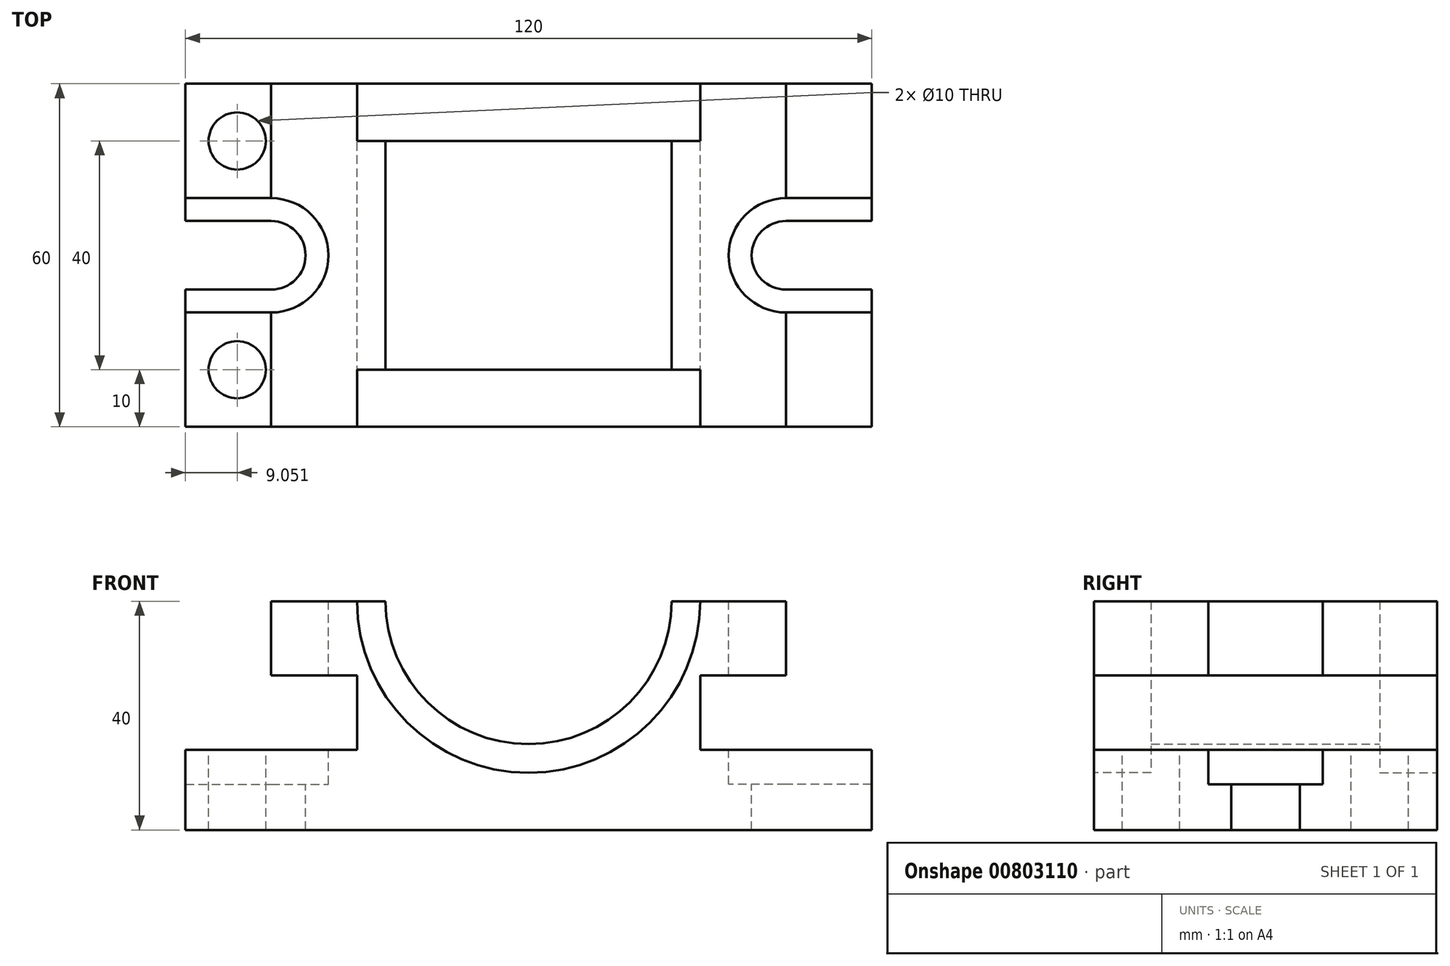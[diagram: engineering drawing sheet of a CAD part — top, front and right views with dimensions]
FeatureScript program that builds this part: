
annotation { "Feature Type Name" : "Feature", "Feature Type Description" : "" }
export const myFeature = defineFeature(function(context is Context, id is Id, definition is map)
    precondition{}
    {
        {
            var Q0;
            Q0=qCreatedBy(makeId("Front.planeOp"),FACE);
            var sketch = newSketch(context, id + "F0", { "sketchPlane" : qUnion([Q0])});
            skLineSegment(sketch, "E0.bottom", {"start": v(45, 20) * mm, "end": v(25, 20) * mm});
            skLineSegment(sketch, "E0.top", {"start": v(60, -20) * mm, "end": v(-60, -20) * mm});
            skLineSegment(sketch, "E0.left", {"start": v(60, -6) * mm, "end": v(60, -20) * mm});
            skPoint(sketch, "E0.middle", {"position": v(0, 0) * mm});
            skLineSegment(sketch, "E1.bottom", {"start": v(-45, 7) * mm, "end": v(-30, 7) * mm});
            skLineSegment(sketch, "E1.top", {"start": v(-60, -6) * mm, "end": v(-30, -6) * mm});
            skLineSegment(sketch, "E1.right", {"start": v(-30, 7) * mm, "end": v(-30, -6) * mm});
            skLineSegment(sketch, "E2.trimOffspring", {"start": v(-60, -6) * mm, "end": v(-60, -20) * mm});
            skLineSegment(sketch, "E3", {"start": v(-45, 20) * mm, "end": v(-45, 7) * mm});
            skPoint(sketch, "E0.right.start.orphan", {"position": v(-60, 20) * mm});
            skLineSegment(sketch, "E4.MirrorCS", {"start": v(30, 7) * mm, "end": v(30, -6) * mm});
            skLineSegment(sketch, "E5.MirrorCS", {"start": v(45, 7) * mm, "end": v(30, 7) * mm});
            skLineSegment(sketch, "E6.MirrorCS", {"start": v(45, 20) * mm, "end": v(45, 7) * mm});
            skLineSegment(sketch, "E7.MirrorCS", {"start": v(60, -6) * mm, "end": v(30, -6) * mm});
            skPoint(sketch, "E8.orphan", {"position": v(60, 20) * mm});
            skArc(sketch, "E9", {"start": v(-25, 20) * mm, "mid": v(0, -5) * mm, "end": v(25, 20) * mm});
            skLineSegment(sketch, "E10.trimOffspring", {"start": v(-25, 20) * mm, "end": v(-45, 20) * mm});
            skSolve(sketch);
        }
        {
            var Q0;
            Q0 = qSketchRegion(id + "F0", true);
            extrude(context, id + "F1", {"entities" : qUnion([Q0]), "depth" : 30 * mm, "offsetDistance" : 25 * mm, "hasSecondDirection" : true, "secondDirectionOppositeDirection" : true, "secondDirectionDepth" : 30 * mm});
        }
        {
            var Q0;
            Q0=makeQuery(id+"F1.opExtrude","CAP_FACE",FACE,{"disambiguationData":[OSD([sQuery(id+"F0.wireOp",EDGE,"E0.bottom"),sQuery(id+"F0.wireOp",EDGE,"E0.top"),sQuery(id+"F0.wireOp",EDGE,"E1.bottom"),sQuery(id+"F0.wireOp",EDGE,"E1.top"),sQuery(id+"F0.wireOp",EDGE,"E1.right"),sQuery(id+"F0.wireOp",EDGE,"E2.trimOffspring"),sQuery(id+"F0.wireOp",EDGE,"E3"),sQuery(id+"F0.wireOp",EDGE,"E4.MirrorCS"),sQuery(id+"F0.wireOp",EDGE,"E5.MirrorCS"),sQuery(id+"F0.wireOp",EDGE,"E6.MirrorCS"),sQuery(id+"F0.wireOp",EDGE,"E7.MirrorCS"),sQuery(id+"F0.wireOp",EDGE,"E0.left"),sQuery(id+"F0.wireOp",EDGE,"E9"),sQuery(id+"F0.wireOp",EDGE,"E10.trimOffspring")])],"isStart":false});
            var sketch = newSketch(context, id + "F2", { "sketchPlane" : qUnion([Q0])});
            skArc(sketch, "E11", {"start": v(-30, 20) * mm, "mid": v(0, -10) * mm, "end": v(30, 20) * mm});
            skLineSegment(sketch, "E12", {"start": v(-30, 20) * mm, "end": v(30, 20) * mm});
            skSolve(sketch);
        }
        {
            var Q0;
            {var subQ0=sQuery(id+"F2.wireOp",EDGE,"E11");Q0=makeQuery(id+"F2.imprint","IMPRINT",FACE,{"disambiguationData":[TD([[makeQuery(id+"F2.imprint","IMPRINT",EDGE,{"derivedFrom":subQ0}),1.0]])]});}
            extrude(context, id + "F3", {"entities" : qUnion([Q0]), "operationType" : NewBodyOperationType.REMOVE, "oppositeDirection" : true, "depth" : 10 * mm, "offsetDistance" : 25 * mm});
        }
        {
            var Q0;
            Q0=makeQuery(id+"F1.opExtrude","CAP_FACE",FACE,{"disambiguationData":[OSD([sQuery(id+"F0.wireOp",EDGE,"E0.bottom"),sQuery(id+"F0.wireOp",EDGE,"E0.top"),sQuery(id+"F0.wireOp",EDGE,"E1.bottom"),sQuery(id+"F0.wireOp",EDGE,"E1.top"),sQuery(id+"F0.wireOp",EDGE,"E1.right"),sQuery(id+"F0.wireOp",EDGE,"E2.trimOffspring"),sQuery(id+"F0.wireOp",EDGE,"E3"),sQuery(id+"F0.wireOp",EDGE,"E4.MirrorCS"),sQuery(id+"F0.wireOp",EDGE,"E5.MirrorCS"),sQuery(id+"F0.wireOp",EDGE,"E6.MirrorCS"),sQuery(id+"F0.wireOp",EDGE,"E7.MirrorCS"),sQuery(id+"F0.wireOp",EDGE,"E0.left"),sQuery(id+"F0.wireOp",EDGE,"E9"),sQuery(id+"F0.wireOp",EDGE,"E10.trimOffspring")])],"isStart":true});
            var sketch = newSketch(context, id + "F4", { "sketchPlane" : qUnion([Q0])});
            skArc(sketch, "E13", {"start": v(-30, 20) * mm, "mid": v(0, -10) * mm, "end": v(30, 20) * mm});
            skLineSegment(sketch, "E14", {"start": v(-30, 20) * mm, "end": v(30, 20) * mm});
            skSolve(sketch);
        }
        {
            var Q0;
            {var subQ0=sQuery(id+"F4.wireOp",EDGE,"E13");Q0=makeQuery(id+"F4.imprint","IMPRINT",FACE,{"disambiguationData":[TD([[makeQuery(id+"F4.imprint","IMPRINT",EDGE,{"derivedFrom":subQ0}),1.0]])]});}
            extrude(context, id + "F5", {"entities" : qUnion([Q0]), "operationType" : NewBodyOperationType.REMOVE, "oppositeDirection" : true, "depth" : 10 * mm, "offsetDistance" : 25 * mm});
        }
        {
            var Q0;
            Q0=makeQuery(id+"F1.opExtrude","SWEPT_FACE",FACE,{"disambiguationData":[OSD([sQuery(id+"F0.wireOp",EDGE,"E10.trimOffspring")])]});
            var sketch = newSketch(context, id + "F6", { "sketchPlane" : qUnion([Q0])});
            skLineSegment(sketch, "E15.bottom", {"start": v(-78.4, 10) * mm, "end": v(-45, 10) * mm});
            skLineSegment(sketch, "E15.top", {"start": v(-78.4, -10) * mm, "end": v(-45, -10) * mm});
            skLineSegment(sketch, "E15.left", {"start": v(-78.4, 10) * mm, "end": v(-78.4, -10) * mm});
            skArc(sketch, "E16", {"start": v(-45, -10) * mm, "mid": v(-35, 0) * mm, "end": v(-45, 10) * mm});
            skArc(sketch, "E17.MirrorC", {"start": v(45, -10) * mm, "mid": v(35, 0) * mm, "end": v(45, 10) * mm});
            skLineSegment(sketch, "E18.MirrorCS", {"start": v(78.4, 10) * mm, "end": v(45, 10) * mm});
            skLineSegment(sketch, "E19.MirrorCS", {"start": v(78.4, -10) * mm, "end": v(45, -10) * mm});
            skLineSegment(sketch, "E20.MirrorCS", {"start": v(78.4, 10) * mm, "end": v(78.4, -10) * mm});
            skSolve(sketch);
        }
        {
            var Q0;
            Q0 = qSketchRegion(id + "F6", true);
            extrude(context, id + "F7", {"entities" : qUnion([Q0]), "operationType" : NewBodyOperationType.REMOVE, "oppositeDirection" : true, "depth" : 32 * mm, "offsetDistance" : 25 * mm});
        }
        {
            var Q0;
            Q0=makeQuery(id+"F1.opExtrude","SWEPT_FACE",FACE,{"disambiguationData":[OSD([sQuery(id+"F0.wireOp",EDGE,"E1.top")])]});
            var sketch = newSketch(context, id + "F8", { "sketchPlane" : qUnion([Q0])});
            skLineSegment(sketch, "E21.bottom", {"start": v(-64, 6) * mm, "end": v(-45, 6) * mm});
            skLineSegment(sketch, "E21.top", {"start": v(-64, -6) * mm, "end": v(-45, -6) * mm});
            skLineSegment(sketch, "E21.left", {"start": v(-64, 6) * mm, "end": v(-64, -6) * mm});
            skPoint(sketch, "E21.middle", {"position": v(-45.31, 0) * mm});
            skArc(sketch, "E22", {"start": v(-45, -6) * mm, "mid": v(-39, 0) * mm, "end": v(-45, 6) * mm});
            skPoint(sketch, "E23.orphan", {"position": v(-26.62, 6) * mm});
            skPoint(sketch, "E24.orphan", {"position": v(-26.62, -6) * mm});
            skArc(sketch, "E25.MirrorCS", {"start": v(45, -6) * mm, "mid": v(39, 0) * mm, "end": v(45, 6) * mm});
            skLineSegment(sketch, "E26.MirrorCS", {"start": v(64, -6) * mm, "end": v(45, -6) * mm});
            skLineSegment(sketch, "E27.MirrorCS", {"start": v(64, 6) * mm, "end": v(45, 6) * mm});
            skLineSegment(sketch, "E28.MirrorCS", {"start": v(64, 6) * mm, "end": v(64, -6) * mm});
            skSolve(sketch);
        }
        {
            var Q0;
            Q0 = qSketchRegion(id + "F8", true);
            extrude(context, id + "F9", {"entities" : qUnion([Q0]), "operationType" : NewBodyOperationType.REMOVE, "oppositeDirection" : true, "depth" : 14 * mm, "offsetDistance" : 25 * mm});
        }
        {
            var Q0;
            Q0=makeQuery(id+"F1.opExtrude","SWEPT_FACE",FACE,{"disambiguationData":[OSD([sQuery(id+"F0.wireOp",EDGE,"E1.top")])]});
            var sketch = newSketch(context, id + "F10", { "sketchPlane" : qUnion([Q0])});
            skCircle(sketch, "E29", {"center": v(-50.95, 20) * mm, "radius": 5 * mm});
            skPoint(sketch, "E29.centerSnap0", {"position": v(-60, 20) * mm});
            skCircle(sketch, "E30.MirrorC", {"center": v(-50.95, -20) * mm, "radius": 5 * mm});
            skSolve(sketch);
        }
        {
            var Q0;
            Q0 = qSketchRegion(id + "F10", true);
            extrude(context, id + "F11", {"entities" : qUnion([Q0]), "operationType" : NewBodyOperationType.REMOVE, "oppositeDirection" : true, "depth" : 15 * mm, "offsetDistance" : 25 * mm});
        }
    });
